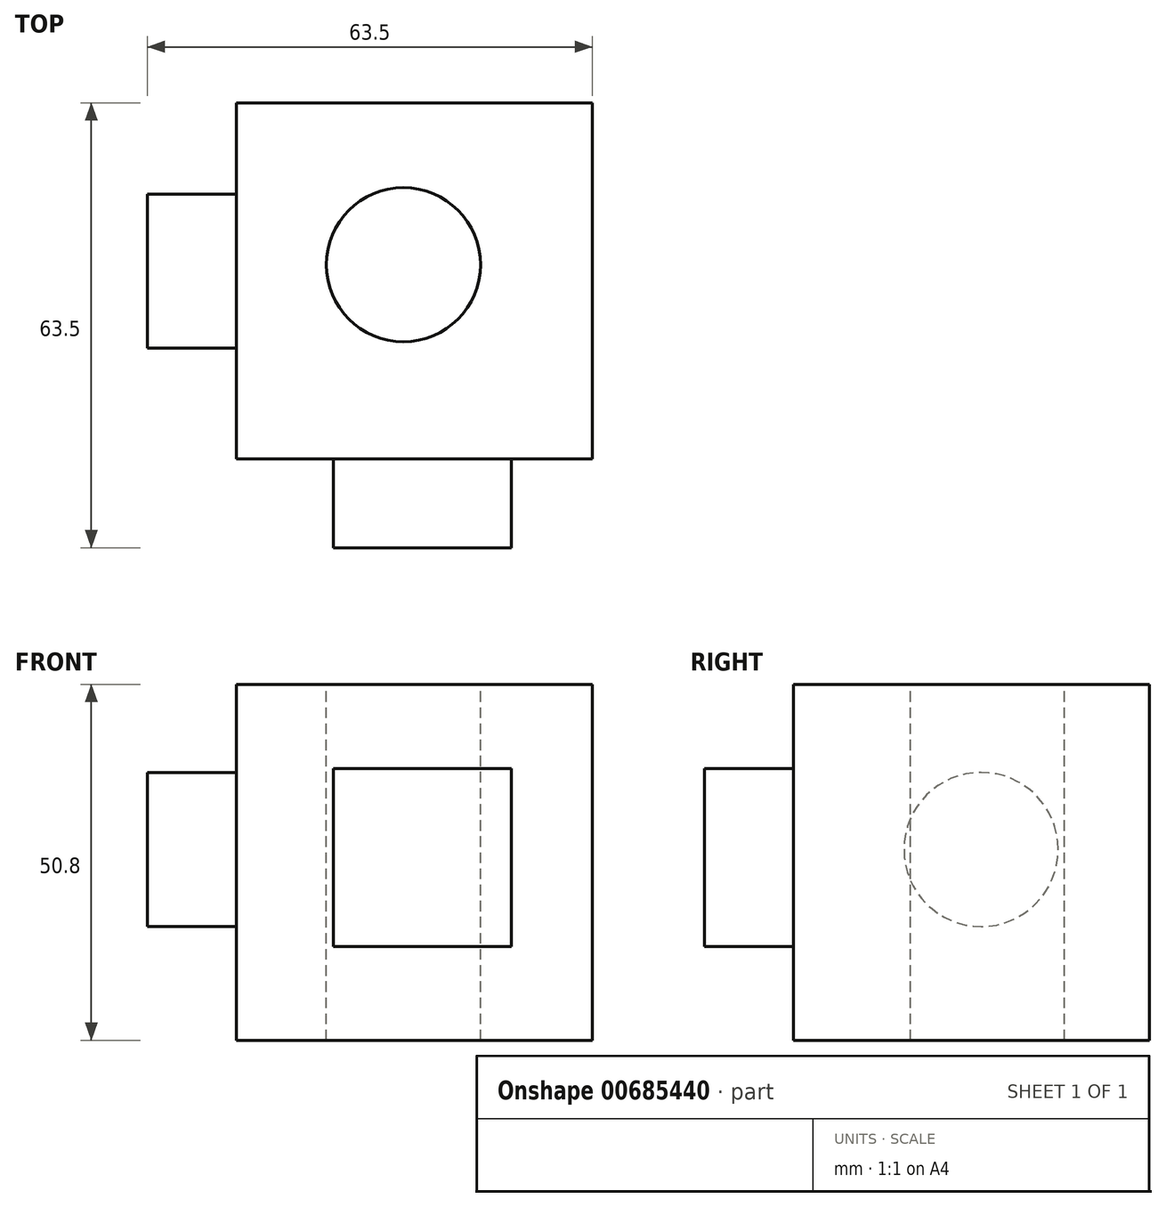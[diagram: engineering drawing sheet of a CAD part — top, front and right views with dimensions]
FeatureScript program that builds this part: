
annotation { "Feature Type Name" : "Feature", "Feature Type Description" : "" }
export const myFeature = defineFeature(function(context is Context, id is Id, definition is map)
    precondition{}
    {
        {
            var Q0;
            Q0=qCreatedBy(makeId("Front.planeOp"),FACE);
            var sketch = newSketch(context, id + "F0", { "sketchPlane" : qUnion([Q0])});
            skLineSegment(sketch, "E0.bottom", {"start": v(-47.33, 46.7) * mm, "end": v(3.47, 46.7) * mm});
            skLineSegment(sketch, "E0.top", {"start": v(-47.33, -4.1) * mm, "end": v(3.47, -4.1) * mm});
            skLineSegment(sketch, "E0.left", {"start": v(-47.33, 46.7) * mm, "end": v(-47.33, -4.1) * mm});
            skLineSegment(sketch, "E0.right", {"start": v(3.47, 46.7) * mm, "end": v(3.47, -4.1) * mm});
            skSolve(sketch);
        }
        {
            var Q0;
            Q0=makeQuery(id+"F0.imprint","IMPRINT",FACE,{"disambiguationData":[TD([[makeQuery(id+"F0.imprint","IMPRINT",EDGE,{"derivedFrom":sQuery(id+"F0.wireOp",EDGE,"E0.bottom")}),-1.0]])]});
            extrude(context, id + "F1", {"entities" : qUnion([Q0]), "depth" : 50.8 * mm, "offsetDistance" : 25.4 * mm});
        }
        {
            var Q0;
            Q0=makeQuery(id+"F1.opExtrude","CAP_FACE",FACE,{"disambiguationData":[OSD([sQuery(id+"F0.wireOp",EDGE,"E0.bottom"),sQuery(id+"F0.wireOp",EDGE,"E0.top"),sQuery(id+"F0.wireOp",EDGE,"E0.left"),sQuery(id+"F0.wireOp",EDGE,"E0.right")])],"isStart":false});
            var sketch = newSketch(context, id + "F2", { "sketchPlane" : qUnion([Q0])});
            skLineSegment(sketch, "E1.bottom", {"start": v(-33.5, 34.65) * mm, "end": v(-8.1, 34.65) * mm});
            skLineSegment(sketch, "E1.top", {"start": v(-33.5, 9.25) * mm, "end": v(-8.1, 9.25) * mm});
            skLineSegment(sketch, "E1.left", {"start": v(-33.5, 34.65) * mm, "end": v(-33.5, 9.25) * mm});
            skLineSegment(sketch, "E1.right", {"start": v(-8.1, 34.65) * mm, "end": v(-8.1, 9.25) * mm});
            skSolve(sketch);
        }
        {
            var Q0;
            Q0=makeQuery(id+"F2.imprint","IMPRINT",FACE,{"disambiguationData":[TD([[makeQuery(id+"F2.imprint","IMPRINT",EDGE,{"derivedFrom":sQuery(id+"F2.wireOp",EDGE,"E1.bottom")}),-1.0]])]});
            extrude(context, id + "F3", {"entities" : qUnion([Q0]), "operationType" : NewBodyOperationType.ADD, "depth" : 12.7 * mm, "offsetDistance" : 25.4 * mm});
        }
        {
            var Q0;
            Q0=makeQuery(id+"F1.opExtrude","SWEPT_FACE",FACE,{"disambiguationData":[OSD([sQuery(id+"F0.wireOp",EDGE,"E0.bottom")])]});
            var sketch = newSketch(context, id + "F4", { "sketchPlane" : qUnion([Q0])});
            skCircle(sketch, "E2", {"center": v(-23.5, -23.12) * mm, "radius": 11 * mm});
            skSolve(sketch);
        }
        {
            var Q0;
            Q0 = qSketchRegion(id + "F4", true);
            extrude(context, id + "F5", {"entities" : qUnion([Q0]), "operationType" : NewBodyOperationType.REMOVE, "oppositeDirection" : true, "depth" : 50.8 * mm, "offsetDistance" : 25.4 * mm});
        }
        {
            var Q0;
            Q0=makeQuery(id+"F1.opExtrude","SWEPT_FACE",FACE,{"disambiguationData":[OSD([sQuery(id+"F0.wireOp",EDGE,"E0.left")])]});
            var sketch = newSketch(context, id + "F6", { "sketchPlane" : qUnion([Q0])});
            skCircle(sketch, "E3", {"center": v(24.02, 23.12) * mm, "radius": 11 * mm});
            skSolve(sketch);
        }
        {
            var Q0;
            Q0 = qSketchRegion(id + "F6", true);
            extrude(context, id + "F7", {"entities" : qUnion([Q0]), "operationType" : NewBodyOperationType.ADD, "depth" : 12.7 * mm, "offsetDistance" : 25.4 * mm});
        }
    });
